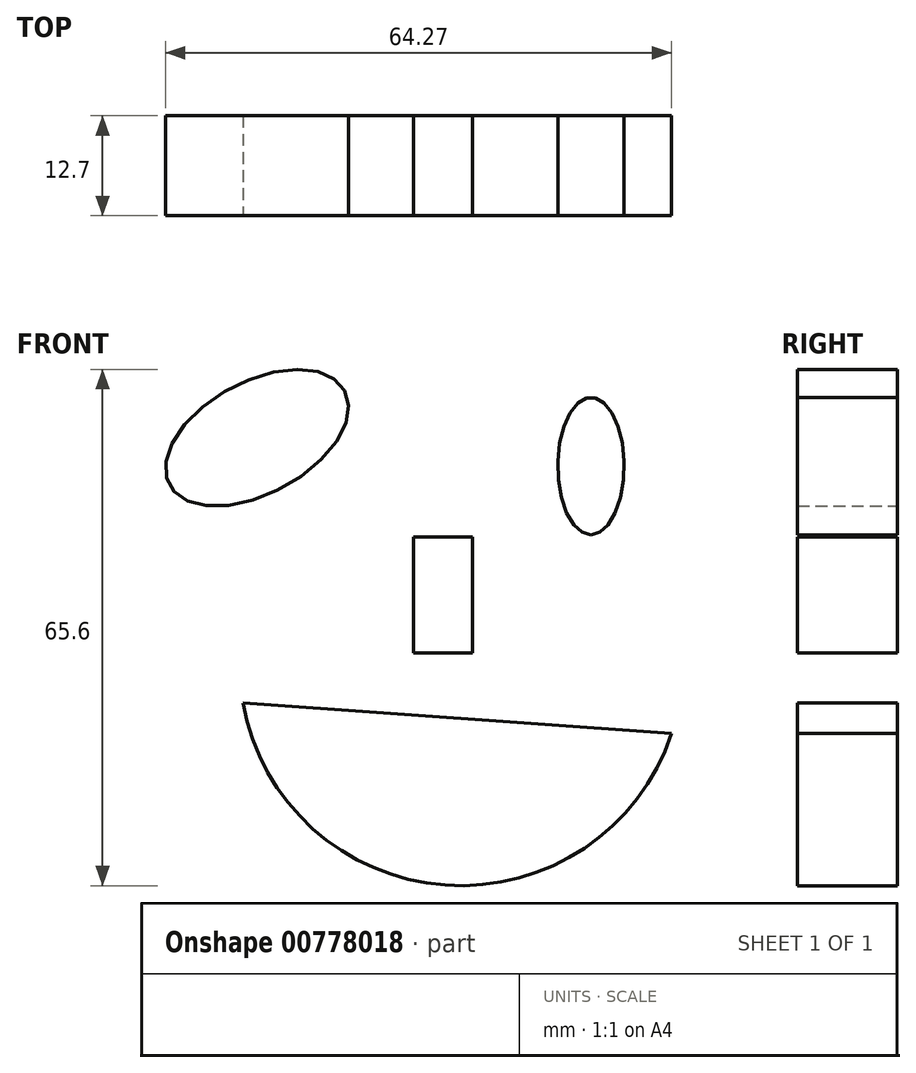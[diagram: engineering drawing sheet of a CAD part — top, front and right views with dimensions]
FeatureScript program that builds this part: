
annotation { "Feature Type Name" : "Feature", "Feature Type Description" : "" }
export const myFeature = defineFeature(function(context is Context, id is Id, definition is map)
    precondition{}
    {
        {
            var Q0;
            Q0=qCreatedBy(makeId("Front.planeOp"),FACE);
            var sketch = newSketch(context, id + "F0", { "sketchPlane" : qUnion([Q0])});
            skCircle(sketch, "E0", {"center": v(0, 0) * mm, "radius": 45.43 * mm});
            skSolve(sketch);
        }
        {
            var Q0;
            Q0 = qSketchRegion(id + "F0", true);
            extrude(context, id + "F1", {"entities" : qUnion([Q0]), "oppositeDirection" : true, "depth" : 12.7 * mm, "offsetDistance" : 25.4 * mm});
        }
        {
            var Q0;
            Q0=makeQuery(id+"FgwIhKSESKiZuQj_1.boolean.opBoolean","MERGE",FACE,{"derivedFrom":[makeQuery(id+"F1.opExtrude","CAP_FACE",FACE,{"disambiguationData":[OSD([sQuery(id+"F0.wireOp",EDGE,"E0")])],"isStart":true}),makeQuery(id+"FgwIhKSESKiZuQj_1.opExtrude","CAP_FACE",FACE,{"disambiguationData":[OSD([sQuery(id+"FjOcbqjAQqpzrZT_1.wireOp",EDGE,"62QwtwuR-H8g8-cW5y-Lfsu-I8jLr8XL91Kw")])],"isStart":true}),makeQuery(id+"FgwIhKSESKiZuQj_1.opExtrude","CAP_FACE",FACE,{"disambiguationData":[OSD([sQuery(id+"FjOcbqjAQqpzrZT_1.wireOp",EDGE,"qE7MHOMQ-wTZI-PtPx-cZIk-toVg54sYGwBV")])],"isStart":true})]});
            var sketch = newSketch(context, id + "F2", { "sketchPlane" : qUnion([Q0])});
            skFitSpline(sketch, "E1", {"points": [v(-26.02, 34.14) * mm, v(-34.74, 72.34) * mm, v(-23.01, 60.3) * mm, v(-14.29, 72.04) * mm, v(-7.07, 49.48) * mm, v(0, 63.92) * mm, v(10.68, 53.09) * mm, v(14.29, 69.03) * mm, v(19.4, 49.18) * mm, v(32.03, 71.14) * mm, v(40.46, 61.51) * mm, v(29.03, 44.37) * mm, v(44.97, 49.18) * mm, v(44.37, 37.75) * mm, v(63.02, 47.98) * mm, v(35.04, 24.51) * mm], "startDerivative": vector(-186.22, 650.86) * mm, "endDerivative": vector(-520.28, -426.17) * mm});
            skLineSegment(sketch, "E2", {"start": v(-26.02, 34.14) * mm, "end": v(35.04, 24.51) * mm});
            skSolve(sketch);
        }
        {
            var Q0;
            Q0 = qSketchRegion(id + "F2", true);
            extrude(context, id + "F3", {"entities" : qUnion([Q0]), "operationType" : NewBodyOperationType.ADD, "oppositeDirection" : true, "depth" : 12.7 * mm, "offsetDistance" : 25.4 * mm});
        }
        {
            var Q0;
            Q0=makeQuery(id+"F1.opExtrude","CAP_FACE",FACE,{"disambiguationData":[OSD([sQuery(id+"F0.wireOp",EDGE,"E0")])],"isStart":true});
            var sketch = newSketch(context, id + "F4", { "sketchPlane" : qUnion([Q0])});
            skEllipse(sketch, "E3", {"center": v(-23.61, 20) * mm, "majorRadius": 12.65 * mm, "minorRadius": 7.12 * mm, "majorAxis": v(0.88, 0.48)});
            skEllipse(sketch, "E4", {"center": v(18.8, 16.4) * mm, "majorRadius": 8.72 * mm, "minorRadius": 4.21 * mm, "majorAxis": v(0, -1)});
            skLineSegment(sketch, "E5.bottom", {"start": v(3.76, -7.37) * mm, "end": v(-3.76, -7.37) * mm});
            skLineSegment(sketch, "E5.top", {"start": v(3.76, 7.37) * mm, "end": v(-3.76, 7.37) * mm});
            skLineSegment(sketch, "E5.left", {"start": v(3.76, -7.37) * mm, "end": v(3.76, 7.37) * mm});
            skLineSegment(sketch, "E5.right", {"start": v(-3.76, -7.37) * mm, "end": v(-3.76, 7.37) * mm});
            skPoint(sketch, "E5.middle", {"position": v(0, 0) * mm});
            skArc(sketch, "E6", {"start": v(-25.42, -13.69) * mm, "mid": v(0.28, -36.84) * mm, "end": v(29.03, -17.6) * mm});
            skLineSegment(sketch, "E7", {"start": v(-25.42, -13.69) * mm, "end": v(29.03, -17.6) * mm});
            skSolve(sketch);
        }
        {
            var Q0;
            Q0=makeQuery(id+"F3.boolean.opBoolean","MERGE",FACE,{"derivedFrom":[makeQuery(id+"FgwIhKSESKiZuQj_1.boolean.opBoolean","MERGE",FACE,{"derivedFrom":[makeQuery(id+"F1.opExtrude","CAP_FACE",FACE,{"disambiguationData":[OSD([sQuery(id+"F0.wireOp",EDGE,"E0")])],"isStart":true}),makeQuery(id+"FgwIhKSESKiZuQj_1.opExtrude","CAP_FACE",FACE,{"disambiguationData":[OSD([sQuery(id+"FjOcbqjAQqpzrZT_1.wireOp",EDGE,"62QwtwuR-H8g8-cW5y-Lfsu-I8jLr8XL91Kw")])],"isStart":true}),makeQuery(id+"FgwIhKSESKiZuQj_1.opExtrude","CAP_FACE",FACE,{"disambiguationData":[OSD([sQuery(id+"FjOcbqjAQqpzrZT_1.wireOp",EDGE,"qE7MHOMQ-wTZI-PtPx-cZIk-toVg54sYGwBV")])],"isStart":true})]}),makeQuery(id+"F3.opExtrude","CAP_FACE",FACE,{"disambiguationData":[OSD([sQuery(id+"F2.wireOp",EDGE,"E1"),sQuery(id+"F2.wireOp",EDGE,"E2")])],"isStart":true})]});
            var sketch = newSketch(context, id + "F5", { "sketchPlane" : qUnion([Q0])});
            skFitSpline(sketch, "E8", {"points": [v(-20.6, 41.06) * mm, v(0, 30.53) * mm, v(-3.76, 26.92) * mm, v(-20.6, 41.06) * mm]});
            skFitSpline(sketch, "E9", {"points": [v(10.38, 28.73) * mm, v(29.03, 37.15) * mm, v(30.23, 33.54) * mm, v(10.38, 28.73) * mm]});
            skSolve(sketch);
        }
        {
            var Q0;
            Q0 = qSketchRegion(id + "F5", true);
            extrude(context, id + "F6", {"entities" : qUnion([Q0]), "operationType" : NewBodyOperationType.REMOVE, "oppositeDirection" : true, "depth" : 2.54 * mm, "offsetDistance" : 25.4 * mm});
        }
        {
            var Q0;
            Q0 = qSketchRegion(id + "F4", true);
            extrude(context, id + "F7", {"entities" : qUnion([Q0]), "operationType" : NewBodyOperationType.INTERSECT, "oppositeDirection" : true, "depth" : 25.4 * mm, "offsetDistance" : 25.4 * mm});
        }
    });
